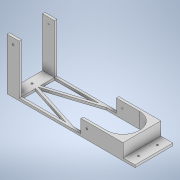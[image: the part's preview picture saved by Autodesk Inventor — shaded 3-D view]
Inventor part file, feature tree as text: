
AUTODESK INVENTOR PART (.ipt)
format: ipt  version: 2020 (Build 240168000, 168)  size: 232,448 bytes
history: native  units: mm
features: sketch x5, other x3, extrude x3, hole x2, mirror x1
ambient origin geometry x8: Origin, YZ Plane, XZ Plane, XY Plane, X Axis, Y Axis, Z Axis, Center Point
bodies: Body1 (feature_tree)
feature tree (14):
  other  "Твердое тело1"
  extrude  "Выдавливание1"  Depth=106.5mm
  extrude  "Выдавливание2"  Depth=10.0mm
  extrude  "Выдавливание3"  Depth=2.0mm TaperAngle=0.0deg
  hole  "Отверстие1"  [1 undecoded]
  mirror  "Зеркальное отражение1"
  hole  "Отверстие2"  [1 undecoded]
  sketch  "Эскиз1"
  sketch  "Эскиз2"
  sketch  "Эскиз3"
  sketch  "Эскиз4"
  sketch  "Эскиз5"
  other  "Проецирование ребер1"
  other  "Проецирование ребер2"
note: 2 required parameter values undecoded (feature->parameter linkage not recoverable at this tier; creation-order binding heuristic only, values carry confidence <= 0.55)
